# Revit family: Loading-Equipment_Dock-levellers_Overhead-Door_Mechanical-Pit-leveler
name_source: partatom
category: Specialty Equipment
units: mm (PartAtom-declared; Revit-internal decimal feet)

## family parameters
Cut with Voids When Loaded = Yes
Host = Face
OmniClass Number = 23.50.70.14.14
OmniClass Title = Manual Dock Levelers
Part Type = Normal
Room Calculation Point = No
Round Connector Dimension = Use Diameter
Shared = No

## types (2) — shared parameters
Default Elevation = 4' - 0"
Length = 8' - 0"
Main Material = Metal - Overhead Door - Steel
Manufacturer = Overhead Door Corporation
Product Page URL = https://www.overheaddoor.com
Product data url = https://www.bimobject.com
Top Plate Material = Metal - Overhead Door - Steel Checker Plate
URL = https://www.overheaddoor.com
z_Real Length = 7' - 3"

## per-type parameters (varying)
| type | Description | Model | Width |
| 6ft Wide - 8ft Length – Extension Spring - Mechanical Pit | Model M68R Mechanical Pit Leveler | Pit Leveler M68R | 6' - 0" |
| 7ft Wide - 8ft Length – Extension Spring - Mechanical Pit | Model M78R Mechanical Pit Leveler | Pit Leveler M78R | 6' - 11" |

## geometry (parser evidence)
native form markers: Sweep x18
no freeform markers — native parametric forms only
